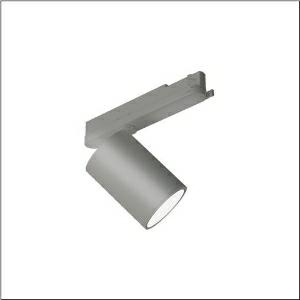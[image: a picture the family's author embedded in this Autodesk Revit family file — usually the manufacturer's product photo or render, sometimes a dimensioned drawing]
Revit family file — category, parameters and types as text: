
# Revit family: spot_31_51sf64mad4b
name_source: partatom
category: Lighting Fixtures
units: mm (PartAtom-declared; Revit-internal decimal feet)

## family parameters
Cut with Voids When Loaded = No
Host = Face
Light Source = No
Part Type = Normal
Room Calculation Point = No
Round Connector Dimension = Use Diameter
Shared = No

## types (1)
- --- (1 x LED, 5250 lm, 41.4 W, 4000K)
    Apparent Load = 41 VA
    CIE Flux Codes = 93 97 100 100 100
    Color Rendering = 90
    Color Temperature = 4000K
    Default Elevation = 1800 mm
    Description = Spot 31, directional spotlight, light control with lens, of PMMA, LED rated luminous flux: 5.040lm, light colour: 940, control gear: ECG Multilumen, with 3-phase adapter, mains connection: 220..240V, AC, 50/60Hz, of aluminium, metallic grey (RAL 9006), length: 213mm, diameter: 90mm, protection rating (complete): IP20, insulation class (complete): insulation class I (protective earthing), certification: CE, impact resistance: IK02, permissible ambient temperature for indoor applications: -20..+40°C, packaging unit: 1 piece
    Height = 175 mm
    Lamp = 1 x LED
    Lamp Light Flux = 5250 lm
    Lamp Power = 41.4 W
    Lamp count = 1
    Length = 90 mm
    Luminous efficacy = 127 lm/W
    Manufacturer = Siteco
    ModVariant = No
    Model = 51SF64MAD4B
    Mounting Place = Ceiling
    Mounting Type = Pendant
    Number of Poles = 1
    OnlyDefault = Yes
    Power Factor = 1
    Product Name = Spot 31
    Product group = directional spotlight
    ProductGroupID = 905
    Protection Class = Protection class I
    Protection Degree = IP 20
    RLX_Detail_Level = 1
    RLX_Emergency_Light_Flux = 0 lm
    RLX_Emergency_Type = 0
    RLX_Emergency_Type_DB = No
    RlxData = <blob elided: 20069 chars, md5=1ccb616d>
    Socket = socket
    Standby Power = 0 W
    System Light Flux = 5250 lm
    System Power = 41 W
    Type Comments = factory setting: luminous flux: 100 % | (ON | ON | ON | ON) | 1050 mA
    Type Image = l_1273725.jpg
    URL = http://relux.com
    VarID = @adj_145713
    Voltage = 0 V
    Weight = 0.00 kg
    Width = 0 mm  [stored 0 ft]

note: [stored X ft] marks values corroborated as IEEE doubles in the binary element streams (Revit-internal decimal feet)

## geometry (parser evidence)
native form markers: Blend x4, Sweep x12
no freeform markers — native parametric forms only
